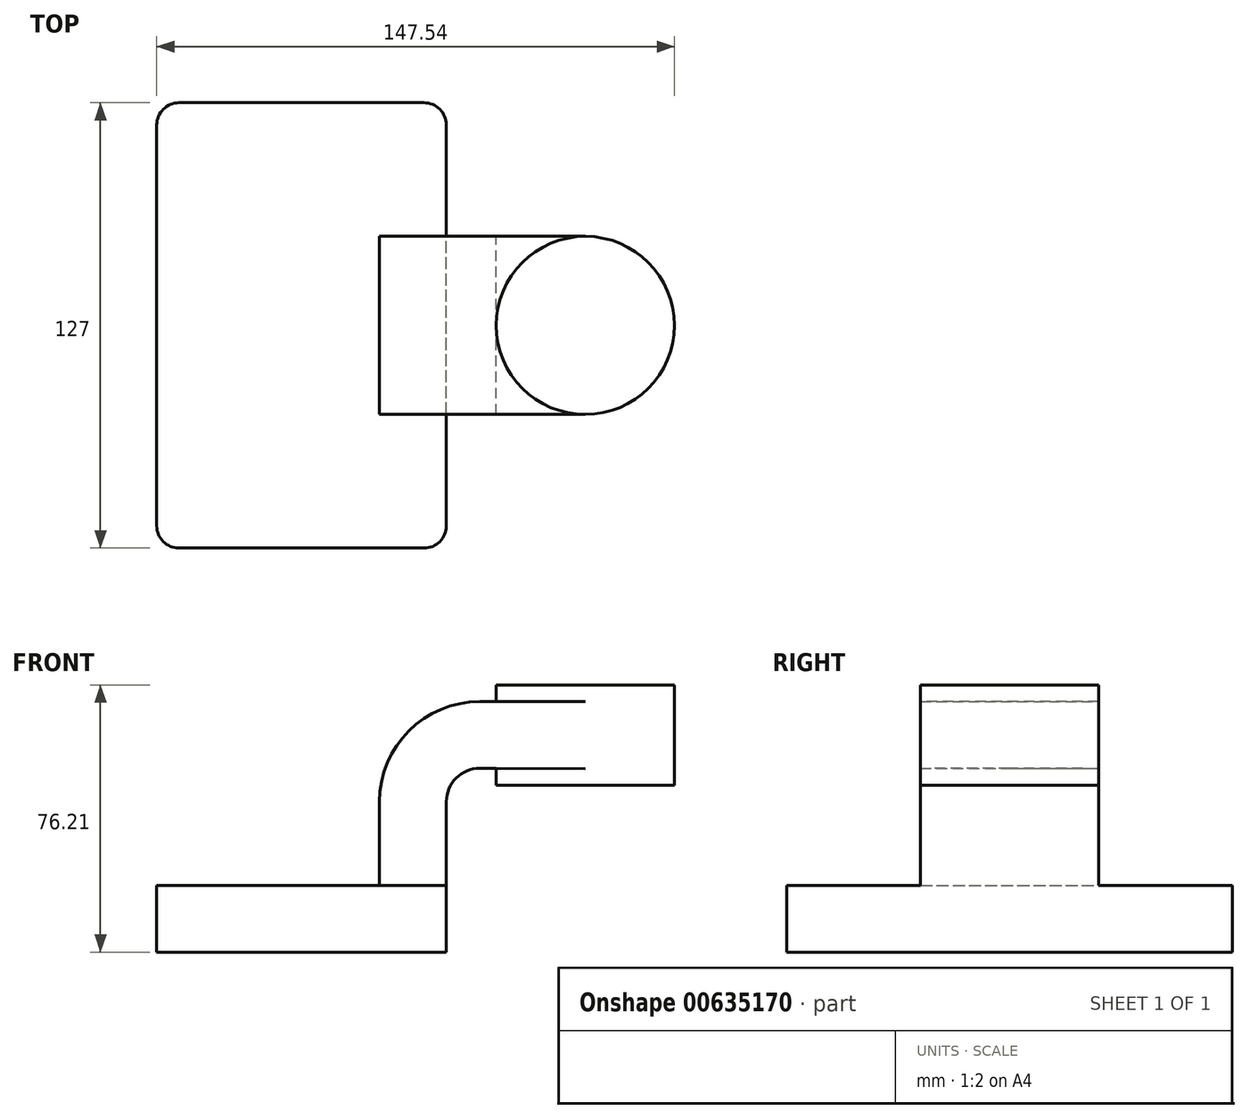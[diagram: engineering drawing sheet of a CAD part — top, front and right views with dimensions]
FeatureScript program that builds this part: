
annotation { "Feature Type Name" : "Feature", "Feature Type Description" : "" }
export const myFeature = defineFeature(function(context is Context, id is Id, definition is map)
    precondition{}
    {
        {
            var Q0;
            Q0=qCreatedBy(makeId("Front.planeOp"),FACE);
            var sketch = newSketch(context, id + "F0", { "sketchPlane" : qUnion([Q0])});
            skLineSegment(sketch, "E0.bottom", {"start": v(41.28, -9.52) * mm, "end": v(-41.28, -9.53) * mm});
            skLineSegment(sketch, "E0.top", {"start": v(41.28, 9.53) * mm, "end": v(-41.28, 9.52) * mm});
            skLineSegment(sketch, "E0.left", {"start": v(41.28, -9.52) * mm, "end": v(41.28, 9.53) * mm});
            skLineSegment(sketch, "E0.right", {"start": v(-41.28, -9.53) * mm, "end": v(-41.28, 9.52) * mm});
            skPoint(sketch, "E0.middle", {"position": v(0, 0) * mm});
            skLineSegment(sketch, "E1.bottom", {"start": v(106.27, 38.1) * mm, "end": v(55.47, 38.1) * mm});
            skLineSegment(sketch, "E1.top", {"start": v(106.27, 66.68) * mm, "end": v(55.47, 66.68) * mm});
            skLineSegment(sketch, "E1.left", {"start": v(106.27, 38.1) * mm, "end": v(106.27, 66.68) * mm});
            skLineSegment(sketch, "E1.right", {"start": v(55.47, 38.1) * mm, "end": v(55.47, 66.68) * mm});
            skPoint(sketch, "E1.middle", {"position": v(80.87, 52.39) * mm});
            skLineSegment(sketch, "E2", {"start": v(41.28, 9.53) * mm, "end": v(41.28, 33.36) * mm});
            skArc(sketch, "E3", {"start": v(41.28, 33.36) * mm, "mid": v(44.06, 40.09) * mm, "end": v(50.8, 42.88) * mm});
            skLineSegment(sketch, "E4", {"start": v(50.8, 42.88) * mm, "end": v(70.87, 42.88) * mm});
            skLineSegment(sketch, "E5.0", {"start": v(50.8, 61.93) * mm, "end": v(70.87, 61.93) * mm});
            skArc(sketch, "E5.1", {"start": v(22.23, 33.36) * mm, "mid": v(30.6, 53.56) * mm, "end": v(50.8, 61.93) * mm});
            skLineSegment(sketch, "E5.2", {"start": v(22.23, 9.53) * mm, "end": v(22.23, 33.36) * mm});
            skFitSpline(sketch, "E6", {"points": [v(-41.28, 9.52) * mm, v(50.8, 61.93) * mm], "startDerivative": vector(1.63, 69.14) * mm, "endDerivative": vector(100.64, -0.74) * mm});
            skLineSegment(sketch, "E7", {"start": v(50.8, 61.93) * mm, "end": v(80.87, 61.93) * mm});
            skLineSegment(sketch, "E8", {"start": v(50.8, 42.88) * mm, "end": v(80.87, 42.75) * mm});
            skPoint(sketch, "E9.endSnap0", {"position": v(80.87, 38.1) * mm});
            skLineSegment(sketch, "E10", {"start": v(80.87, 66.68) * mm, "end": v(80.87, 38.1) * mm});
            skSolve(sketch);
        }
        {
            var Q0;
            Q0=makeQuery(id+"F0.imprint","IMPRINT",FACE,{"disambiguationData":[TD([[makeQuery(id+"F0.imprint","IMPRINT",EDGE,{"derivedFrom":sQuery(id+"F0.wireOp",EDGE,"E0.bottom")}),-1.0]])]});
            extrude(context, id + "F1", {"entities" : qUnion([Q0]), "endBound" : BoundingType.SYMMETRIC, "depth" : 127 * mm, "offsetDistance" : 25.4 * mm});
        }
        {
            var Q0;
            {var subQ0=sQuery(id+"F0.wireOp",EDGE,"E7");var subQ1=makeQuery(id+"F0.imprint","IMPRINT",VERTEX,{"derivedFrom":subQ0});Q0=makeQuery(id+"F0.imprint","IMPRINT",FACE,{"disambiguationData":[TD([[makeQuery(id+"F0.imprint","IMPRINT",EDGE,{"disambiguationData":[TD([[subQ1,1.0]])],"derivedFrom":subQ0}),-1.0]])]});}
            var Q1;
            {var subQ1=sQuery(id+"F0.wireOp",EDGE,"E2");Q1=makeQuery(id+"F0.imprint","IMPRINT",FACE,{"disambiguationData":[TD([[makeQuery(id+"F0.imprint","IMPRINT",EDGE,{"derivedFrom":subQ1}),1.0]])]});}
            extrude(context, id + "F2", {"entities" : qUnion([Q0, Q1]), "operationType" : NewBodyOperationType.ADD, "endBound" : BoundingType.SYMMETRIC, "depth" : 50.8 * mm, "offsetDistance" : 25.4 * mm});
        }
        {
            var Q0;
            Q0=makeQuery(id+"F0.imprint","IMPRINT",FACE,{"disambiguationData":[TD([[makeQuery(id+"F0.imprint","IMPRINT",EDGE,{"derivedFrom":sQuery(id+"F0.wireOp",EDGE,"E5.1")}),1.0]])]});
            extrude(context, id + "F3", {"entities" : qUnion([Q0]), "operationType" : NewBodyOperationType.ADD, "endBound" : BoundingType.SYMMETRIC, "depth" : 15.88 * mm, "offsetDistance" : 25.4 * mm});
        }
        {
            var Q0;
            {var subQ0=sQuery(id+"F0.wireOp",EDGE,"E1.left");Q0=makeQuery(id+"F0.imprint","IMPRINT",FACE,{"disambiguationData":[TD([[makeQuery(id+"F0.imprint","IMPRINT",EDGE,{"derivedFrom":subQ0}),1.0]])]});}
            var Q1;
            Q1=sQuery(id+"F0.wireOp",EDGE,"E10");
            revolve(context, id + "F4", {"operationType" : NewBodyOperationType.ADD, "entities" : qUnion([Q0]), "axis" : qUnion([Q1]), "revolveType" : RevolveType.FULL});
        }
        {
            var Q0;
            Q0=makeQuery(id+"F1.opExtrude","CAP_EDGE",EDGE,{"disambiguationData":[OSD([sQuery(id+"F0.wireOp",EDGE,"E0.right")])],"isStart":false});
            var Q1;
            Q1=makeQuery(id+"F1.opExtrude","CAP_EDGE",EDGE,{"disambiguationData":[OSD([sQuery(id+"F0.wireOp",EDGE,"E0.left")])],"isStart":false});
            var Q2;
            Q2=makeQuery(id+"F1.opExtrude","CAP_EDGE",EDGE,{"disambiguationData":[OSD([sQuery(id+"F0.wireOp",EDGE,"E0.left")])],"isStart":true});
            var Q3;
            Q3=makeQuery(id+"F1.opExtrude","CAP_EDGE",EDGE,{"disambiguationData":[OSD([sQuery(id+"F0.wireOp",EDGE,"E0.right")])],"isStart":true});
            fillet(context, id + "F5", {"entities" : qUnion([Q0, Q1, Q2, Q3]), "radius" : 6.35 * mm, "tangentPropagation" : true, "allowEdgeOverflow" : false});
        }
    });
